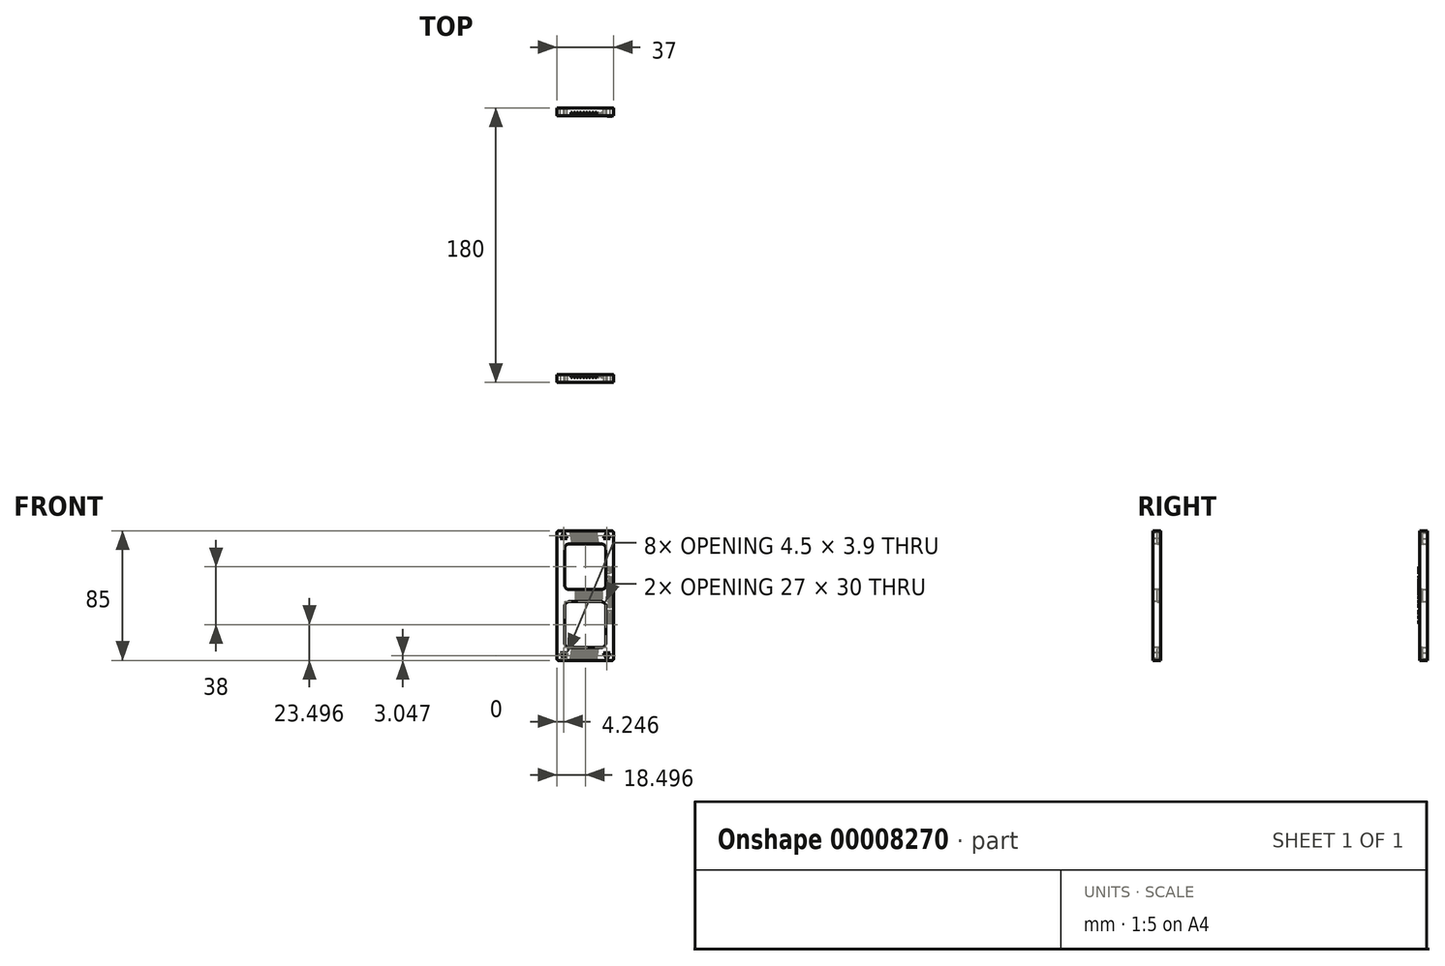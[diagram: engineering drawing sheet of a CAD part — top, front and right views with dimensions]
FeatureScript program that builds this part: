
annotation { "Feature Type Name" : "Feature", "Feature Type Description" : "" }
export const myFeature = defineFeature(function(context is Context, id is Id, definition is map)
    precondition{}
    {
        {
            var Q0;
            Q0=qCreatedBy(makeId("Front.planeOp"),FACE);
            var sketch = newSketch(context, id + "F0", { "sketchPlane" : qUnion([Q0])});
            skLineSegment(sketch, "E0.bottom", {"start": v(-64.24, 55.65) * mm, "end": v(-29.24, 55.65) * mm});
            skLineSegment(sketch, "E0.top", {"start": v(-64.24, -29.35) * mm, "end": v(-29.24, -29.35) * mm});
            skLineSegment(sketch, "E0.left", {"start": v(-65.24, 54.65) * mm, "end": v(-65.24, -28.35) * mm});
            skLineSegment(sketch, "E0.right", {"start": v(-28.24, 54.65) * mm, "end": v(-28.24, -28.35) * mm});
            skLineSegment(sketch, "E1.bottom", {"start": v(-57.24, 47.15) * mm, "end": v(-36.24, 47.15) * mm});
            skLineSegment(sketch, "E1.top", {"start": v(-57.24, 17.15) * mm, "end": v(-36.24, 17.15) * mm});
            skLineSegment(sketch, "E1.left", {"start": v(-60.24, 44.15) * mm, "end": v(-60.24, 20.15) * mm});
            skLineSegment(sketch, "E1.right", {"start": v(-33.24, 44.15) * mm, "end": v(-33.24, 20.15) * mm});
            skPoint(sketch, "E2", {"position": v(-65.24, 13.15) * mm});
            skPoint(sketch, "E3", {"position": v(-28.24, 13.15) * mm});
            skLineSegment(sketch, "E4", {"start": v(-65.24, 13.15) * mm, "end": v(-28.24, 13.15) * mm, "construction": true});
            skPoint(sketch, "E5", {"position": v(-46.74, 13.15) * mm});
            skPoint(sketch, "E6", {"position": v(-46.74, 17.15) * mm});
            skPoint(sketch, "E7", {"position": v(-46.74, 47.15) * mm});
            skLineSegment(sketch, "E8", {"start": v(-46.74, -29.35) * mm, "end": v(-46.74, 55.65) * mm, "construction": true});
            skLineSegment(sketch, "E9.MirrorCS", {"start": v(-57.24, 9.15) * mm, "end": v(-36.24, 9.15) * mm});
            skLineSegment(sketch, "E10.MirrorCS", {"start": v(-33.24, -17.85) * mm, "end": v(-33.24, 6.15) * mm});
            skLineSegment(sketch, "E11.MirrorCS", {"start": v(-57.24, -20.85) * mm, "end": v(-36.24, -20.85) * mm});
            skLineSegment(sketch, "E12.MirrorCS", {"start": v(-60.24, -17.85) * mm, "end": v(-60.24, 6.15) * mm});
            skLineSegment(sketch, "E13", {"start": v(-61, 54.54) * mm, "end": v(-63.24, 50.65) * mm});
            skLineSegment(sketch, "E14", {"start": v(-63.24, 50.65) * mm, "end": v(-58.74, 50.65) * mm});
            skLineSegment(sketch, "E15", {"start": v(-58.74, 50.65) * mm, "end": v(-61, 54.54) * mm});
            skLineSegment(sketch, "E16.MirrorCS", {"start": v(-32.5, 54.54) * mm, "end": v(-30.24, 50.65) * mm});
            skLineSegment(sketch, "E17.MirrorCS", {"start": v(-34.74, 50.65) * mm, "end": v(-32.5, 54.54) * mm});
            skLineSegment(sketch, "E18.MirrorCS", {"start": v(-30.24, 50.65) * mm, "end": v(-34.74, 50.65) * mm});
            skLineSegment(sketch, "E19.MirrorCS", {"start": v(-32.5, -28.25) * mm, "end": v(-30.24, -24.35) * mm});
            skLineSegment(sketch, "E20.MirrorCS", {"start": v(-34.74, -24.35) * mm, "end": v(-32.5, -28.25) * mm});
            skLineSegment(sketch, "E21.MirrorCS", {"start": v(-30.24, -24.35) * mm, "end": v(-34.74, -24.35) * mm});
            skLineSegment(sketch, "E22.MirrorCS", {"start": v(-58.74, -24.35) * mm, "end": v(-61, -28.25) * mm});
            skLineSegment(sketch, "E23.MirrorCS", {"start": v(-61, -28.25) * mm, "end": v(-63.24, -24.35) * mm});
            skLineSegment(sketch, "E24.MirrorCS", {"start": v(-63.24, -24.35) * mm, "end": v(-58.74, -24.35) * mm});
            skPoint(sketch, "E25.visualSharp", {"position": v(-60.24, 47.15) * mm});
            skArc(sketch, "E25.filletArc", {"start": v(-57.24, 47.15) * mm, "mid": v(-59.37, 46.27) * mm, "end": v(-60.24, 44.15) * mm});
            skPoint(sketch, "E26.visualSharp", {"position": v(-33.24, 47.15) * mm});
            skArc(sketch, "E26.filletArc", {"start": v(-33.24, 44.15) * mm, "mid": v(-34.12, 46.27) * mm, "end": v(-36.24, 47.15) * mm});
            skPoint(sketch, "E27.visualSharp", {"position": v(-33.24, 17.15) * mm});
            skArc(sketch, "E27.filletArc", {"start": v(-36.24, 17.15) * mm, "mid": v(-34.12, 18.02) * mm, "end": v(-33.24, 20.15) * mm});
            skPoint(sketch, "E28.visualSharp", {"position": v(-60.24, 17.15) * mm});
            skArc(sketch, "E28.filletArc", {"start": v(-60.24, 20.15) * mm, "mid": v(-59.37, 18.02) * mm, "end": v(-57.24, 17.15) * mm});
            skPoint(sketch, "E29.visualSharp", {"position": v(-33.24, 9.15) * mm});
            skArc(sketch, "E29.filletArc", {"start": v(-33.24, 6.15) * mm, "mid": v(-34.12, 8.27) * mm, "end": v(-36.24, 9.15) * mm});
            skPoint(sketch, "E30.visualSharp", {"position": v(-33.24, -20.85) * mm});
            skArc(sketch, "E30.filletArc", {"start": v(-36.24, -20.85) * mm, "mid": v(-34.12, -19.98) * mm, "end": v(-33.24, -17.85) * mm});
            skPoint(sketch, "E31.visualSharp", {"position": v(-60.24, -20.85) * mm});
            skArc(sketch, "E31.filletArc", {"start": v(-60.24, -17.85) * mm, "mid": v(-59.37, -19.98) * mm, "end": v(-57.24, -20.85) * mm});
            skPoint(sketch, "E32.visualSharp", {"position": v(-60.24, 9.15) * mm});
            skArc(sketch, "E32.filletArc", {"start": v(-57.24, 9.15) * mm, "mid": v(-59.37, 8.27) * mm, "end": v(-60.24, 6.15) * mm});
            skPoint(sketch, "E33.visualSharp", {"position": v(-28.24, 55.65) * mm});
            skArc(sketch, "E33.filletArc", {"start": v(-28.24, 54.65) * mm, "mid": v(-28.54, 55.35) * mm, "end": v(-29.24, 55.65) * mm});
            skPoint(sketch, "E34.visualSharp", {"position": v(-28.24, -29.35) * mm});
            skArc(sketch, "E34.filletArc", {"start": v(-29.24, -29.35) * mm, "mid": v(-28.54, -29.06) * mm, "end": v(-28.24, -28.35) * mm});
            skPoint(sketch, "E35.visualSharp", {"position": v(-65.24, -29.35) * mm});
            skArc(sketch, "E35.filletArc", {"start": v(-65.24, -28.35) * mm, "mid": v(-64.95, -29.06) * mm, "end": v(-64.24, -29.35) * mm});
            skPoint(sketch, "E36.visualSharp", {"position": v(-65.24, 55.65) * mm});
            skArc(sketch, "E36.filletArc", {"start": v(-64.24, 55.65) * mm, "mid": v(-64.95, 55.35) * mm, "end": v(-65.24, 54.65) * mm});
            skSolve(sketch);
        }
        {
            var Q0;
            Q0 = qSketchRegion(id + "F0", true);
            extrude(context, id + "F1", {"entities" : qUnion([Q0]), "depth" : 5 * mm});
        }
        {
            var Q0;
            Q0=makeQuery(id+"F1.opExtrude","CAP_FACE",FACE,{"disambiguationData":[OSD([sQuery(id+"F0.wireOp",EDGE,"E0.bottom"),sQuery(id+"F0.wireOp",EDGE,"E0.top"),sQuery(id+"F0.wireOp",EDGE,"E0.left"),sQuery(id+"F0.wireOp",EDGE,"E0.right")])],"isStart":false});
            var sketch = newSketch(context, id + "F2", { "sketchPlane" : qUnion([Q0])});
            skArc(sketch, "E37", {"start": v(-56.24, -29.35) * mm, "mid": v(-52.51, 13.15) * mm, "end": v(-56.24, 55.65) * mm});
            skLineSegment(sketch, "E38", {"start": v(-56.24, 55.65) * mm, "end": v(-56.24, -29.35) * mm, "construction": true});
            skPoint(sketch, "E39", {"position": v(-56.24, 13.15) * mm});
            skLineSegment(sketch, "E40", {"start": v(-56.24, 13.15) * mm, "end": v(-296.24, 13.15) * mm, "construction": true});
            skArc(sketch, "E41.1.0.0", {"start": v(-55.34, -29.35) * mm, "mid": v(-51.61, 13.15) * mm, "end": v(-55.34, 55.65) * mm});
            skLineSegment(sketch, "E41.direction1", {"start": v(-296.24, 13.15) * mm, "end": v(-295.34, 13.15) * mm, "construction": true});
            skLineSegment(sketch, "E42", {"start": v(-56.24, 55.65) * mm, "end": v(-55.34, 55.65) * mm});
            skLineSegment(sketch, "E43", {"start": v(-56.24, -29.35) * mm, "end": v(-55.34, -29.35) * mm});
            skArc(sketch, "E44.1.0.0", {"start": v(-54.24, -29.35) * mm, "mid": v(-50.51, 13.15) * mm, "end": v(-54.24, 55.65) * mm});
            skArc(sketch, "E44.1.0.1", {"start": v(-53.34, -29.35) * mm, "mid": v(-49.61, 13.15) * mm, "end": v(-53.34, 55.65) * mm});
            skLineSegment(sketch, "E44.1.0.2", {"start": v(-54.24, 55.65) * mm, "end": v(-53.34, 55.65) * mm});
            skLineSegment(sketch, "E44.1.0.3", {"start": v(-54.24, -29.35) * mm, "end": v(-53.34, -29.35) * mm});
            skArc(sketch, "E44.2.0.0", {"start": v(-52.24, -29.35) * mm, "mid": v(-48.51, 13.15) * mm, "end": v(-52.24, 55.65) * mm});
            skArc(sketch, "E44.2.0.1", {"start": v(-51.34, -29.35) * mm, "mid": v(-47.61, 13.15) * mm, "end": v(-51.34, 55.65) * mm});
            skLineSegment(sketch, "E44.2.0.2", {"start": v(-52.24, 55.65) * mm, "end": v(-51.34, 55.65) * mm});
            skLineSegment(sketch, "E44.2.0.3", {"start": v(-52.24, -29.35) * mm, "end": v(-51.34, -29.35) * mm});
            skArc(sketch, "E44.3.0.0", {"start": v(-50.24, -29.35) * mm, "mid": v(-46.51, 13.15) * mm, "end": v(-50.24, 55.65) * mm});
            skArc(sketch, "E44.3.0.1", {"start": v(-49.34, -29.35) * mm, "mid": v(-45.61, 13.15) * mm, "end": v(-49.34, 55.65) * mm});
            skLineSegment(sketch, "E44.3.0.2", {"start": v(-50.24, 55.65) * mm, "end": v(-49.34, 55.65) * mm});
            skLineSegment(sketch, "E44.3.0.3", {"start": v(-50.24, -29.35) * mm, "end": v(-49.34, -29.35) * mm});
            skArc(sketch, "E44.4.0.0", {"start": v(-48.24, -29.35) * mm, "mid": v(-44.51, 13.15) * mm, "end": v(-48.24, 55.65) * mm});
            skArc(sketch, "E44.4.0.1", {"start": v(-47.34, -29.35) * mm, "mid": v(-43.61, 13.15) * mm, "end": v(-47.34, 55.65) * mm});
            skLineSegment(sketch, "E44.4.0.2", {"start": v(-48.24, 55.65) * mm, "end": v(-47.34, 55.65) * mm});
            skLineSegment(sketch, "E44.4.0.3", {"start": v(-48.24, -29.35) * mm, "end": v(-47.34, -29.35) * mm});
            skArc(sketch, "E44.5.0.0", {"start": v(-46.24, -29.35) * mm, "mid": v(-42.51, 13.15) * mm, "end": v(-46.24, 55.65) * mm});
            skArc(sketch, "E44.5.0.1", {"start": v(-45.34, -29.35) * mm, "mid": v(-41.61, 13.15) * mm, "end": v(-45.34, 55.65) * mm});
            skLineSegment(sketch, "E44.5.0.2", {"start": v(-46.24, 55.65) * mm, "end": v(-45.34, 55.65) * mm});
            skLineSegment(sketch, "E44.5.0.3", {"start": v(-46.24, -29.35) * mm, "end": v(-45.34, -29.35) * mm});
            skArc(sketch, "E44.6.0.0", {"start": v(-44.24, -29.35) * mm, "mid": v(-40.51, 13.15) * mm, "end": v(-44.24, 55.65) * mm});
            skArc(sketch, "E44.6.0.1", {"start": v(-43.34, -29.35) * mm, "mid": v(-39.61, 13.15) * mm, "end": v(-43.34, 55.65) * mm});
            skLineSegment(sketch, "E44.6.0.2", {"start": v(-44.24, 55.65) * mm, "end": v(-43.34, 55.65) * mm});
            skLineSegment(sketch, "E44.6.0.3", {"start": v(-44.24, -29.35) * mm, "end": v(-43.34, -29.35) * mm});
            skArc(sketch, "E44.7.0.0", {"start": v(-42.24, -29.35) * mm, "mid": v(-38.51, 13.15) * mm, "end": v(-42.24, 55.65) * mm});
            skArc(sketch, "E44.7.0.1", {"start": v(-41.34, -29.35) * mm, "mid": v(-37.61, 13.15) * mm, "end": v(-41.34, 55.65) * mm});
            skLineSegment(sketch, "E44.7.0.2", {"start": v(-42.24, 55.65) * mm, "end": v(-41.34, 55.65) * mm});
            skLineSegment(sketch, "E44.7.0.3", {"start": v(-42.24, -29.35) * mm, "end": v(-41.34, -29.35) * mm});
            skLineSegment(sketch, "E44.direction1", {"start": v(-296.24, 13.15) * mm, "end": v(-294.24, 13.15) * mm, "construction": true});
            skArc(sketch, "E45.0.8.0", {"start": v(-40.24, -29.35) * mm, "mid": v(-36.51, 13.15) * mm, "end": v(-40.24, 55.65) * mm});
            skArc(sketch, "E45.4.8.0", {"start": v(-39.34, -29.35) * mm, "mid": v(-35.61, 13.15) * mm, "end": v(-39.34, 55.65) * mm});
            skLineSegment(sketch, "E45.8.8.0", {"start": v(-40.24, 55.65) * mm, "end": v(-39.34, 55.65) * mm});
            skLineSegment(sketch, "E45.11.8.0", {"start": v(-40.24, -29.35) * mm, "end": v(-39.34, -29.35) * mm});
            skSolve(sketch);
        }
        {
            var Q0;
            Q0 = qSketchRegion(id + "F2", true);
            extrude(context, id + "F3", {"entities" : qUnion([Q0]), "operationType" : NewBodyOperationType.REMOVE, "oppositeDirection" : true, "depth" : 2 * mm});
        }
        {
            var Q0;
            {var subQ1=sQuery(id+"F0.wireOp",EDGE,"E0.top");var subQ2=sQuery(id+"F2.wireOp",EDGE,"E37");Q0=makeQuery(id+"F3.boolean.opBoolean","COPY",EDGE,{"disambiguationData":[TD([makeQuery(id+"F1.opExtrude","SWEPT_FACE",FACE,{"disambiguationData":[OSD([subQ1])]})])],"derivedFrom":makeQuery(id+"F3.opExtrude","CAP_EDGE",EDGE,{"disambiguationData":[OSD([subQ2])],"isStart":true})});}
            var Q1;
            {var subQ1=sQuery(id+"F0.wireOp",EDGE,"E0.top");var subQ2=sQuery(id+"F2.wireOp",EDGE,"E41.1.0.0");Q1=makeQuery(id+"F3.boolean.opBoolean","COPY",EDGE,{"disambiguationData":[TD([makeQuery(id+"F1.opExtrude","SWEPT_FACE",FACE,{"disambiguationData":[OSD([subQ1])]})])],"derivedFrom":makeQuery(id+"F3.opExtrude","CAP_EDGE",EDGE,{"disambiguationData":[OSD([subQ2])],"isStart":true})});}
            var Q2;
            {var subQ1=sQuery(id+"F0.wireOp",EDGE,"E0.top");var subQ2=sQuery(id+"F2.wireOp",EDGE,"E44.1.0.0");Q2=makeQuery(id+"F3.boolean.opBoolean","COPY",EDGE,{"disambiguationData":[TD([makeQuery(id+"F1.opExtrude","SWEPT_FACE",FACE,{"disambiguationData":[OSD([subQ1])]})])],"derivedFrom":makeQuery(id+"F3.opExtrude","CAP_EDGE",EDGE,{"disambiguationData":[OSD([subQ2])],"isStart":true})});}
            var Q3;
            {var subQ1=sQuery(id+"F0.wireOp",EDGE,"E0.top");var subQ2=sQuery(id+"F2.wireOp",EDGE,"E44.1.0.1");Q3=makeQuery(id+"F3.boolean.opBoolean","COPY",EDGE,{"disambiguationData":[TD([makeQuery(id+"F1.opExtrude","SWEPT_FACE",FACE,{"disambiguationData":[OSD([subQ1])]})])],"derivedFrom":makeQuery(id+"F3.opExtrude","CAP_EDGE",EDGE,{"disambiguationData":[OSD([subQ2])],"isStart":true})});}
            var Q4;
            {var subQ1=sQuery(id+"F0.wireOp",EDGE,"E0.top");var subQ2=sQuery(id+"F2.wireOp",EDGE,"E44.2.0.0");Q4=makeQuery(id+"F3.boolean.opBoolean","COPY",EDGE,{"disambiguationData":[TD([makeQuery(id+"F1.opExtrude","SWEPT_FACE",FACE,{"disambiguationData":[OSD([subQ1])]})])],"derivedFrom":makeQuery(id+"F3.opExtrude","CAP_EDGE",EDGE,{"disambiguationData":[OSD([subQ2])],"isStart":true})});}
            var Q5;
            {var subQ1=sQuery(id+"F0.wireOp",EDGE,"E0.top");var subQ2=sQuery(id+"F2.wireOp",EDGE,"E44.2.0.1");Q5=makeQuery(id+"F3.boolean.opBoolean","COPY",EDGE,{"disambiguationData":[TD([makeQuery(id+"F1.opExtrude","SWEPT_FACE",FACE,{"disambiguationData":[OSD([subQ1])]})])],"derivedFrom":makeQuery(id+"F3.opExtrude","CAP_EDGE",EDGE,{"disambiguationData":[OSD([subQ2])],"isStart":true})});}
            var Q6;
            {var subQ1=sQuery(id+"F0.wireOp",EDGE,"E0.top");var subQ2=sQuery(id+"F2.wireOp",EDGE,"E44.3.0.0");Q6=makeQuery(id+"F3.boolean.opBoolean","COPY",EDGE,{"disambiguationData":[TD([makeQuery(id+"F1.opExtrude","SWEPT_FACE",FACE,{"disambiguationData":[OSD([subQ1])]})])],"derivedFrom":makeQuery(id+"F3.opExtrude","CAP_EDGE",EDGE,{"disambiguationData":[OSD([subQ2])],"isStart":true})});}
            var Q7;
            {var subQ1=sQuery(id+"F0.wireOp",EDGE,"E0.top");var subQ2=sQuery(id+"F2.wireOp",EDGE,"E44.3.0.1");Q7=makeQuery(id+"F3.boolean.opBoolean","COPY",EDGE,{"disambiguationData":[TD([makeQuery(id+"F1.opExtrude","SWEPT_FACE",FACE,{"disambiguationData":[OSD([subQ1])]})])],"derivedFrom":makeQuery(id+"F3.opExtrude","CAP_EDGE",EDGE,{"disambiguationData":[OSD([subQ2])],"isStart":true})});}
            var Q8;
            {var subQ1=sQuery(id+"F0.wireOp",EDGE,"E0.top");var subQ2=sQuery(id+"F2.wireOp",EDGE,"E44.4.0.0");Q8=makeQuery(id+"F3.boolean.opBoolean","COPY",EDGE,{"disambiguationData":[TD([makeQuery(id+"F1.opExtrude","SWEPT_FACE",FACE,{"disambiguationData":[OSD([subQ1])]})])],"derivedFrom":makeQuery(id+"F3.opExtrude","CAP_EDGE",EDGE,{"disambiguationData":[OSD([subQ2])],"isStart":true})});}
            var Q9;
            {var subQ1=sQuery(id+"F0.wireOp",EDGE,"E0.top");var subQ2=sQuery(id+"F2.wireOp",EDGE,"E44.4.0.1");Q9=makeQuery(id+"F3.boolean.opBoolean","COPY",EDGE,{"disambiguationData":[TD([makeQuery(id+"F1.opExtrude","SWEPT_FACE",FACE,{"disambiguationData":[OSD([subQ1])]})])],"derivedFrom":makeQuery(id+"F3.opExtrude","CAP_EDGE",EDGE,{"disambiguationData":[OSD([subQ2])],"isStart":true})});}
            var Q10;
            {var subQ1=sQuery(id+"F0.wireOp",EDGE,"E0.top");var subQ2=sQuery(id+"F2.wireOp",EDGE,"E44.5.0.0");Q10=makeQuery(id+"F3.boolean.opBoolean","COPY",EDGE,{"disambiguationData":[TD([makeQuery(id+"F1.opExtrude","SWEPT_FACE",FACE,{"disambiguationData":[OSD([subQ1])]})])],"derivedFrom":makeQuery(id+"F3.opExtrude","CAP_EDGE",EDGE,{"disambiguationData":[OSD([subQ2])],"isStart":true})});}
            var Q11;
            {var subQ1=sQuery(id+"F0.wireOp",EDGE,"E0.top");var subQ2=sQuery(id+"F2.wireOp",EDGE,"E44.5.0.1");Q11=makeQuery(id+"F3.boolean.opBoolean","COPY",EDGE,{"disambiguationData":[TD([makeQuery(id+"F1.opExtrude","SWEPT_FACE",FACE,{"disambiguationData":[OSD([subQ1])]})])],"derivedFrom":makeQuery(id+"F3.opExtrude","CAP_EDGE",EDGE,{"disambiguationData":[OSD([subQ2])],"isStart":true})});}
            var Q12;
            {var subQ1=sQuery(id+"F0.wireOp",EDGE,"E0.top");var subQ2=sQuery(id+"F2.wireOp",EDGE,"E44.6.0.0");Q12=makeQuery(id+"F3.boolean.opBoolean","COPY",EDGE,{"disambiguationData":[TD([makeQuery(id+"F1.opExtrude","SWEPT_FACE",FACE,{"disambiguationData":[OSD([subQ1])]})])],"derivedFrom":makeQuery(id+"F3.opExtrude","CAP_EDGE",EDGE,{"disambiguationData":[OSD([subQ2])],"isStart":true})});}
            var Q13;
            {var subQ1=sQuery(id+"F0.wireOp",EDGE,"E0.top");var subQ2=sQuery(id+"F2.wireOp",EDGE,"E44.6.0.1");Q13=makeQuery(id+"F3.boolean.opBoolean","COPY",EDGE,{"disambiguationData":[TD([makeQuery(id+"F1.opExtrude","SWEPT_FACE",FACE,{"disambiguationData":[OSD([subQ1])]})])],"derivedFrom":makeQuery(id+"F3.opExtrude","CAP_EDGE",EDGE,{"disambiguationData":[OSD([subQ2])],"isStart":true})});}
            var Q14;
            {var subQ1=sQuery(id+"F0.wireOp",EDGE,"E0.top");var subQ2=sQuery(id+"F2.wireOp",EDGE,"E44.7.0.0");Q14=makeQuery(id+"F3.boolean.opBoolean","COPY",EDGE,{"disambiguationData":[TD([makeQuery(id+"F1.opExtrude","SWEPT_FACE",FACE,{"disambiguationData":[OSD([subQ1])]})])],"derivedFrom":makeQuery(id+"F3.opExtrude","CAP_EDGE",EDGE,{"disambiguationData":[OSD([subQ2])],"isStart":true})});}
            var Q15;
            {var subQ1=sQuery(id+"F0.wireOp",EDGE,"E0.top");var subQ2=sQuery(id+"F2.wireOp",EDGE,"E44.7.0.1");Q15=makeQuery(id+"F3.boolean.opBoolean","COPY",EDGE,{"disambiguationData":[TD([makeQuery(id+"F1.opExtrude","SWEPT_FACE",FACE,{"disambiguationData":[OSD([subQ1])]})])],"derivedFrom":makeQuery(id+"F3.opExtrude","CAP_EDGE",EDGE,{"disambiguationData":[OSD([subQ2])],"isStart":true})});}
            var Q16;
            {var subQ1=sQuery(id+"F0.wireOp",EDGE,"E0.top");var subQ2=sQuery(id+"F2.wireOp",EDGE,"E45.0.8.0");Q16=makeQuery(id+"F3.boolean.opBoolean","COPY",EDGE,{"disambiguationData":[TD([makeQuery(id+"F1.opExtrude","SWEPT_FACE",FACE,{"disambiguationData":[OSD([subQ1])]})])],"derivedFrom":makeQuery(id+"F3.opExtrude","CAP_EDGE",EDGE,{"disambiguationData":[OSD([subQ2])],"isStart":true})});}
            var Q17;
            {var subQ1=sQuery(id+"F0.wireOp",EDGE,"E1.top");var subQ2=sQuery(id+"F2.wireOp",EDGE,"E41.1.0.0");Q17=makeQuery(id+"F3.boolean.opBoolean","COPY",EDGE,{"disambiguationData":[TD([makeQuery(id+"F1.opExtrude","SWEPT_FACE",FACE,{"disambiguationData":[OSD([subQ1])]})])],"derivedFrom":makeQuery(id+"F3.opExtrude","CAP_EDGE",EDGE,{"disambiguationData":[OSD([subQ2])],"isStart":true})});}
            var Q18;
            {var subQ1=sQuery(id+"F0.wireOp",EDGE,"E1.top");var subQ2=sQuery(id+"F2.wireOp",EDGE,"E44.1.0.0");Q18=makeQuery(id+"F3.boolean.opBoolean","COPY",EDGE,{"disambiguationData":[TD([makeQuery(id+"F1.opExtrude","SWEPT_FACE",FACE,{"disambiguationData":[OSD([subQ1])]})])],"derivedFrom":makeQuery(id+"F3.opExtrude","CAP_EDGE",EDGE,{"disambiguationData":[OSD([subQ2])],"isStart":true})});}
            var Q19;
            {var subQ1=sQuery(id+"F0.wireOp",EDGE,"E1.top");var subQ2=sQuery(id+"F2.wireOp",EDGE,"E44.1.0.1");Q19=makeQuery(id+"F3.boolean.opBoolean","COPY",EDGE,{"disambiguationData":[TD([makeQuery(id+"F1.opExtrude","SWEPT_FACE",FACE,{"disambiguationData":[OSD([subQ1])]})])],"derivedFrom":makeQuery(id+"F3.opExtrude","CAP_EDGE",EDGE,{"disambiguationData":[OSD([subQ2])],"isStart":true})});}
            var Q20;
            {var subQ1=sQuery(id+"F0.wireOp",EDGE,"E1.top");var subQ2=sQuery(id+"F2.wireOp",EDGE,"E44.2.0.0");Q20=makeQuery(id+"F3.boolean.opBoolean","COPY",EDGE,{"disambiguationData":[TD([makeQuery(id+"F1.opExtrude","SWEPT_FACE",FACE,{"disambiguationData":[OSD([subQ1])]})])],"derivedFrom":makeQuery(id+"F3.opExtrude","CAP_EDGE",EDGE,{"disambiguationData":[OSD([subQ2])],"isStart":true})});}
            var Q21;
            {var subQ1=sQuery(id+"F0.wireOp",EDGE,"E1.top");var subQ2=sQuery(id+"F2.wireOp",EDGE,"E44.2.0.1");Q21=makeQuery(id+"F3.boolean.opBoolean","COPY",EDGE,{"disambiguationData":[TD([makeQuery(id+"F1.opExtrude","SWEPT_FACE",FACE,{"disambiguationData":[OSD([subQ1])]})])],"derivedFrom":makeQuery(id+"F3.opExtrude","CAP_EDGE",EDGE,{"disambiguationData":[OSD([subQ2])],"isStart":true})});}
            var Q22;
            {var subQ1=sQuery(id+"F0.wireOp",EDGE,"E1.top");var subQ2=sQuery(id+"F2.wireOp",EDGE,"E44.3.0.0");Q22=makeQuery(id+"F3.boolean.opBoolean","COPY",EDGE,{"disambiguationData":[TD([makeQuery(id+"F1.opExtrude","SWEPT_FACE",FACE,{"disambiguationData":[OSD([subQ1])]})])],"derivedFrom":makeQuery(id+"F3.opExtrude","CAP_EDGE",EDGE,{"disambiguationData":[OSD([subQ2])],"isStart":true})});}
            var Q23;
            {var subQ1=sQuery(id+"F0.wireOp",EDGE,"E1.top");var subQ2=sQuery(id+"F2.wireOp",EDGE,"E44.3.0.1");Q23=makeQuery(id+"F3.boolean.opBoolean","COPY",EDGE,{"disambiguationData":[TD([makeQuery(id+"F1.opExtrude","SWEPT_FACE",FACE,{"disambiguationData":[OSD([subQ1])]})])],"derivedFrom":makeQuery(id+"F3.opExtrude","CAP_EDGE",EDGE,{"disambiguationData":[OSD([subQ2])],"isStart":true})});}
            var Q24;
            {var subQ1=sQuery(id+"F0.wireOp",EDGE,"E1.top");var subQ2=sQuery(id+"F2.wireOp",EDGE,"E44.4.0.0");Q24=makeQuery(id+"F3.boolean.opBoolean","COPY",EDGE,{"disambiguationData":[TD([makeQuery(id+"F1.opExtrude","SWEPT_FACE",FACE,{"disambiguationData":[OSD([subQ1])]})])],"derivedFrom":makeQuery(id+"F3.opExtrude","CAP_EDGE",EDGE,{"disambiguationData":[OSD([subQ2])],"isStart":true})});}
            var Q25;
            {var subQ1=sQuery(id+"F0.wireOp",EDGE,"E1.top");var subQ2=sQuery(id+"F2.wireOp",EDGE,"E44.4.0.1");Q25=makeQuery(id+"F3.boolean.opBoolean","COPY",EDGE,{"disambiguationData":[TD([makeQuery(id+"F1.opExtrude","SWEPT_FACE",FACE,{"disambiguationData":[OSD([subQ1])]})])],"derivedFrom":makeQuery(id+"F3.opExtrude","CAP_EDGE",EDGE,{"disambiguationData":[OSD([subQ2])],"isStart":true})});}
            var Q26;
            {var subQ1=sQuery(id+"F0.wireOp",EDGE,"E1.top");var subQ2=sQuery(id+"F2.wireOp",EDGE,"E44.5.0.0");Q26=makeQuery(id+"F3.boolean.opBoolean","COPY",EDGE,{"disambiguationData":[TD([makeQuery(id+"F1.opExtrude","SWEPT_FACE",FACE,{"disambiguationData":[OSD([subQ1])]})])],"derivedFrom":makeQuery(id+"F3.opExtrude","CAP_EDGE",EDGE,{"disambiguationData":[OSD([subQ2])],"isStart":true})});}
            var Q27;
            {var subQ1=sQuery(id+"F0.wireOp",EDGE,"E1.top");var subQ2=sQuery(id+"F2.wireOp",EDGE,"E44.5.0.1");Q27=makeQuery(id+"F3.boolean.opBoolean","COPY",EDGE,{"disambiguationData":[TD([makeQuery(id+"F1.opExtrude","SWEPT_FACE",FACE,{"disambiguationData":[OSD([subQ1])]})])],"derivedFrom":makeQuery(id+"F3.opExtrude","CAP_EDGE",EDGE,{"disambiguationData":[OSD([subQ2])],"isStart":true})});}
            var Q28;
            {var subQ1=sQuery(id+"F0.wireOp",EDGE,"E1.top");var subQ2=sQuery(id+"F2.wireOp",EDGE,"E44.6.0.0");Q28=makeQuery(id+"F3.boolean.opBoolean","COPY",EDGE,{"disambiguationData":[TD([makeQuery(id+"F1.opExtrude","SWEPT_FACE",FACE,{"disambiguationData":[OSD([subQ1])]})])],"derivedFrom":makeQuery(id+"F3.opExtrude","CAP_EDGE",EDGE,{"disambiguationData":[OSD([subQ2])],"isStart":true})});}
            var Q29;
            {var subQ1=sQuery(id+"F0.wireOp",EDGE,"E1.top");var subQ2=sQuery(id+"F2.wireOp",EDGE,"E44.6.0.1");Q29=makeQuery(id+"F3.boolean.opBoolean","COPY",EDGE,{"disambiguationData":[TD([makeQuery(id+"F1.opExtrude","SWEPT_FACE",FACE,{"disambiguationData":[OSD([subQ1])]})])],"derivedFrom":makeQuery(id+"F3.opExtrude","CAP_EDGE",EDGE,{"disambiguationData":[OSD([subQ2])],"isStart":true})});}
            var Q30;
            {var subQ1=sQuery(id+"F0.wireOp",EDGE,"E1.top");var subQ2=sQuery(id+"F2.wireOp",EDGE,"E44.7.0.0");Q30=makeQuery(id+"F3.boolean.opBoolean","COPY",EDGE,{"disambiguationData":[TD([makeQuery(id+"F1.opExtrude","SWEPT_FACE",FACE,{"disambiguationData":[OSD([subQ1])]})])],"derivedFrom":makeQuery(id+"F3.opExtrude","CAP_EDGE",EDGE,{"disambiguationData":[OSD([subQ2])],"isStart":true})});}
            var Q31;
            {var subQ1=sQuery(id+"F0.wireOp",EDGE,"E1.top");var subQ2=sQuery(id+"F2.wireOp",EDGE,"E44.7.0.1");Q31=makeQuery(id+"F3.boolean.opBoolean","COPY",EDGE,{"disambiguationData":[TD([makeQuery(id+"F1.opExtrude","SWEPT_FACE",FACE,{"disambiguationData":[OSD([subQ1])]})])],"derivedFrom":makeQuery(id+"F3.opExtrude","CAP_EDGE",EDGE,{"disambiguationData":[OSD([subQ2])],"isStart":true})});}
            var Q32;
            {var subQ1=sQuery(id+"F0.wireOp",EDGE,"E1.top");var subQ2=sQuery(id+"F2.wireOp",EDGE,"E45.0.8.0");Q32=makeQuery(id+"F3.boolean.opBoolean","COPY",EDGE,{"disambiguationData":[TD([makeQuery(id+"F1.opExtrude","SWEPT_FACE",FACE,{"disambiguationData":[OSD([subQ1])]})])],"derivedFrom":makeQuery(id+"F3.opExtrude","CAP_EDGE",EDGE,{"disambiguationData":[OSD([subQ2])],"isStart":true})});}
            var Q33;
            {var subQ0=sQuery(id+"F0.wireOp",EDGE,"E0.bottom");var subQ1=sQuery(id+"F2.wireOp",EDGE,"E37");Q33=makeQuery(id+"F3.boolean.opBoolean","COPY",EDGE,{"disambiguationData":[TD([makeQuery(id+"F1.opExtrude","SWEPT_FACE",FACE,{"disambiguationData":[OSD([subQ0])]})])],"derivedFrom":makeQuery(id+"F3.opExtrude","CAP_EDGE",EDGE,{"disambiguationData":[OSD([subQ1])],"isStart":true})});}
            var Q34;
            {var subQ1=sQuery(id+"F0.wireOp",EDGE,"E1.top");var subQ2=sQuery(id+"F2.wireOp",EDGE,"E37");Q34=makeQuery(id+"F3.boolean.opBoolean","COPY",EDGE,{"disambiguationData":[TD([makeQuery(id+"F1.opExtrude","SWEPT_FACE",FACE,{"disambiguationData":[OSD([subQ1])]})])],"derivedFrom":makeQuery(id+"F3.opExtrude","CAP_EDGE",EDGE,{"disambiguationData":[OSD([subQ2])],"isStart":true})});}
            var Q35;
            {var subQ1=sQuery(id+"F0.wireOp",EDGE,"E27.filletArc");var subQ2=sQuery(id+"F2.wireOp",EDGE,"E45.4.8.0");Q35=makeQuery(id+"F3.boolean.opBoolean","COPY",EDGE,{"disambiguationData":[TD([makeQuery(id+"F1.opExtrude","SWEPT_FACE",FACE,{"disambiguationData":[OSD([subQ1])]})])],"derivedFrom":makeQuery(id+"F3.opExtrude","CAP_EDGE",EDGE,{"disambiguationData":[OSD([subQ2])],"isStart":true})});}
            var Q36;
            {var subQ1=sQuery(id+"F0.wireOp",EDGE,"E0.top");var subQ2=sQuery(id+"F2.wireOp",EDGE,"E45.4.8.0");Q36=makeQuery(id+"F3.boolean.opBoolean","COPY",EDGE,{"disambiguationData":[TD([makeQuery(id+"F1.opExtrude","SWEPT_FACE",FACE,{"disambiguationData":[OSD([subQ1])]})])],"derivedFrom":makeQuery(id+"F3.opExtrude","CAP_EDGE",EDGE,{"disambiguationData":[OSD([subQ2])],"isStart":true})});}
            var Q37;
            Q37=makeQuery(id+"F3.boolean.opBoolean","INTERSECT",EDGE,{"derivedFrom":[makeQuery(id+"F1.opExtrude","SWEPT_FACE",FACE,{"disambiguationData":[OSD([sQuery(id+"F0.wireOp",EDGE,"E1.bottom")])]}),makeQuery(id+"F3.opExtrude","SWEPT_FACE",FACE,{"disambiguationData":[OSD([sQuery(id+"F2.wireOp",EDGE,"E37")])]})]});
            var Q38;
            {var subQ0=sQuery(id+"F0.wireOp",EDGE,"E0.bottom");var subQ2=sQuery(id+"F2.wireOp",EDGE,"E44.1.0.0");Q38=makeQuery(id+"F3.boolean.opBoolean","COPY",EDGE,{"disambiguationData":[TD([makeQuery(id+"F1.opExtrude","SWEPT_FACE",FACE,{"disambiguationData":[OSD([subQ0])]})])],"derivedFrom":makeQuery(id+"F3.opExtrude","CAP_EDGE",EDGE,{"disambiguationData":[OSD([subQ2])],"isStart":true})});}
            var Q39;
            {var subQ0=sQuery(id+"F0.wireOp",EDGE,"E0.bottom");var subQ1=sQuery(id+"F2.wireOp",EDGE,"E44.1.0.1");Q39=makeQuery(id+"F3.boolean.opBoolean","COPY",EDGE,{"disambiguationData":[TD([makeQuery(id+"F1.opExtrude","SWEPT_FACE",FACE,{"disambiguationData":[OSD([subQ0])]})])],"derivedFrom":makeQuery(id+"F3.opExtrude","CAP_EDGE",EDGE,{"disambiguationData":[OSD([subQ1])],"isStart":true})});}
            var Q40;
            {var subQ0=sQuery(id+"F0.wireOp",EDGE,"E0.bottom");var subQ2=sQuery(id+"F2.wireOp",EDGE,"E44.2.0.1");Q40=makeQuery(id+"F3.boolean.opBoolean","COPY",EDGE,{"disambiguationData":[TD([makeQuery(id+"F1.opExtrude","SWEPT_FACE",FACE,{"disambiguationData":[OSD([subQ0])]})])],"derivedFrom":makeQuery(id+"F3.opExtrude","CAP_EDGE",EDGE,{"disambiguationData":[OSD([subQ2])],"isStart":true})});}
            var Q41;
            {var subQ0=sQuery(id+"F0.wireOp",EDGE,"E0.bottom");var subQ1=sQuery(id+"F2.wireOp",EDGE,"E44.3.0.0");Q41=makeQuery(id+"F3.boolean.opBoolean","COPY",EDGE,{"disambiguationData":[TD([makeQuery(id+"F1.opExtrude","SWEPT_FACE",FACE,{"disambiguationData":[OSD([subQ0])]})])],"derivedFrom":makeQuery(id+"F3.opExtrude","CAP_EDGE",EDGE,{"disambiguationData":[OSD([subQ1])],"isStart":true})});}
            var Q42;
            {var subQ0=sQuery(id+"F0.wireOp",EDGE,"E0.bottom");var subQ1=sQuery(id+"F2.wireOp",EDGE,"E44.4.0.0");Q42=makeQuery(id+"F3.boolean.opBoolean","COPY",EDGE,{"disambiguationData":[TD([makeQuery(id+"F1.opExtrude","SWEPT_FACE",FACE,{"disambiguationData":[OSD([subQ0])]})])],"derivedFrom":makeQuery(id+"F3.opExtrude","CAP_EDGE",EDGE,{"disambiguationData":[OSD([subQ1])],"isStart":true})});}
            var Q43;
            {var subQ0=sQuery(id+"F0.wireOp",EDGE,"E0.bottom");var subQ2=sQuery(id+"F2.wireOp",EDGE,"E44.4.0.1");Q43=makeQuery(id+"F3.boolean.opBoolean","COPY",EDGE,{"disambiguationData":[TD([makeQuery(id+"F1.opExtrude","SWEPT_FACE",FACE,{"disambiguationData":[OSD([subQ0])]})])],"derivedFrom":makeQuery(id+"F3.opExtrude","CAP_EDGE",EDGE,{"disambiguationData":[OSD([subQ2])],"isStart":true})});}
            var Q44;
            {var subQ0=sQuery(id+"F0.wireOp",EDGE,"E0.bottom");var subQ2=sQuery(id+"F2.wireOp",EDGE,"E44.5.0.0");Q44=makeQuery(id+"F3.boolean.opBoolean","COPY",EDGE,{"disambiguationData":[TD([makeQuery(id+"F1.opExtrude","SWEPT_FACE",FACE,{"disambiguationData":[OSD([subQ0])]})])],"derivedFrom":makeQuery(id+"F3.opExtrude","CAP_EDGE",EDGE,{"disambiguationData":[OSD([subQ2])],"isStart":true})});}
            var Q45;
            {var subQ0=sQuery(id+"F0.wireOp",EDGE,"E0.bottom");var subQ2=sQuery(id+"F2.wireOp",EDGE,"E44.5.0.1");Q45=makeQuery(id+"F3.boolean.opBoolean","COPY",EDGE,{"disambiguationData":[TD([makeQuery(id+"F1.opExtrude","SWEPT_FACE",FACE,{"disambiguationData":[OSD([subQ0])]})])],"derivedFrom":makeQuery(id+"F3.opExtrude","CAP_EDGE",EDGE,{"disambiguationData":[OSD([subQ2])],"isStart":true})});}
            var Q46;
            {var subQ0=sQuery(id+"F0.wireOp",EDGE,"E0.bottom");var subQ2=sQuery(id+"F2.wireOp",EDGE,"E44.6.0.0");Q46=makeQuery(id+"F3.boolean.opBoolean","COPY",EDGE,{"disambiguationData":[TD([makeQuery(id+"F1.opExtrude","SWEPT_FACE",FACE,{"disambiguationData":[OSD([subQ0])]})])],"derivedFrom":makeQuery(id+"F3.opExtrude","CAP_EDGE",EDGE,{"disambiguationData":[OSD([subQ2])],"isStart":true})});}
            var Q47;
            {var subQ0=sQuery(id+"F0.wireOp",EDGE,"E0.bottom");var subQ2=sQuery(id+"F2.wireOp",EDGE,"E44.6.0.1");Q47=makeQuery(id+"F3.boolean.opBoolean","COPY",EDGE,{"disambiguationData":[TD([makeQuery(id+"F1.opExtrude","SWEPT_FACE",FACE,{"disambiguationData":[OSD([subQ0])]})])],"derivedFrom":makeQuery(id+"F3.opExtrude","CAP_EDGE",EDGE,{"disambiguationData":[OSD([subQ2])],"isStart":true})});}
            var Q48;
            {var subQ0=sQuery(id+"F0.wireOp",EDGE,"E0.bottom");var subQ2=sQuery(id+"F2.wireOp",EDGE,"E44.7.0.0");Q48=makeQuery(id+"F3.boolean.opBoolean","COPY",EDGE,{"disambiguationData":[TD([makeQuery(id+"F1.opExtrude","SWEPT_FACE",FACE,{"disambiguationData":[OSD([subQ0])]})])],"derivedFrom":makeQuery(id+"F3.opExtrude","CAP_EDGE",EDGE,{"disambiguationData":[OSD([subQ2])],"isStart":true})});}
            var Q49;
            {var subQ0=sQuery(id+"F0.wireOp",EDGE,"E0.bottom");var subQ2=sQuery(id+"F2.wireOp",EDGE,"E44.7.0.1");Q49=makeQuery(id+"F3.boolean.opBoolean","COPY",EDGE,{"disambiguationData":[TD([makeQuery(id+"F1.opExtrude","SWEPT_FACE",FACE,{"disambiguationData":[OSD([subQ0])]})])],"derivedFrom":makeQuery(id+"F3.opExtrude","CAP_EDGE",EDGE,{"disambiguationData":[OSD([subQ2])],"isStart":true})});}
            var Q50;
            {var subQ0=sQuery(id+"F0.wireOp",EDGE,"E0.bottom");var subQ2=sQuery(id+"F2.wireOp",EDGE,"E45.0.8.0");Q50=makeQuery(id+"F3.boolean.opBoolean","COPY",EDGE,{"disambiguationData":[TD([makeQuery(id+"F1.opExtrude","SWEPT_FACE",FACE,{"disambiguationData":[OSD([subQ0])]})])],"derivedFrom":makeQuery(id+"F3.opExtrude","CAP_EDGE",EDGE,{"disambiguationData":[OSD([subQ2])],"isStart":true})});}
            var Q51;
            {var subQ0=sQuery(id+"F0.wireOp",EDGE,"E0.bottom");var subQ2=sQuery(id+"F2.wireOp",EDGE,"E45.4.8.0");Q51=makeQuery(id+"F3.boolean.opBoolean","COPY",EDGE,{"disambiguationData":[TD([makeQuery(id+"F1.opExtrude","SWEPT_FACE",FACE,{"disambiguationData":[OSD([subQ0])]})])],"derivedFrom":makeQuery(id+"F3.opExtrude","CAP_EDGE",EDGE,{"disambiguationData":[OSD([subQ2])],"isStart":true})});}
            var Q52;
            {var subQ0=sQuery(id+"F0.wireOp",EDGE,"E0.bottom");var subQ1=sQuery(id+"F2.wireOp",EDGE,"E44.4.0.0");Q52=makeQuery(id+"F3.boolean.opBoolean","COPY",EDGE,{"disambiguationData":[TD([makeQuery(id+"F1.opExtrude","SWEPT_FACE",FACE,{"disambiguationData":[OSD([subQ0])]})])],"derivedFrom":makeQuery(id+"F3.opExtrude","CAP_EDGE",EDGE,{"disambiguationData":[OSD([subQ1])],"isStart":true})});}
            var Q53;
            {var subQ0=sQuery(id+"F0.wireOp",EDGE,"E0.bottom");var subQ1=sQuery(id+"F2.wireOp",EDGE,"E41.1.0.0");Q53=makeQuery(id+"F3.boolean.opBoolean","COPY",EDGE,{"disambiguationData":[TD([makeQuery(id+"F1.opExtrude","SWEPT_FACE",FACE,{"disambiguationData":[OSD([subQ0])]})])],"derivedFrom":makeQuery(id+"F3.opExtrude","CAP_EDGE",EDGE,{"disambiguationData":[OSD([subQ1])],"isStart":true})});}
            var Q54;
            {var subQ0=sQuery(id+"F0.wireOp",EDGE,"E0.bottom");var subQ2=sQuery(id+"F2.wireOp",EDGE,"E44.3.0.1");Q54=makeQuery(id+"F3.boolean.opBoolean","COPY",EDGE,{"disambiguationData":[TD([makeQuery(id+"F1.opExtrude","SWEPT_FACE",FACE,{"disambiguationData":[OSD([subQ0])]})])],"derivedFrom":makeQuery(id+"F3.opExtrude","CAP_EDGE",EDGE,{"disambiguationData":[OSD([subQ2])],"isStart":true})});}
            chamfer(context, id + "F4", {"entities" : qUnion([Q0, Q1, Q2, Q3, Q4, Q5, Q6, Q7, Q8, Q9, Q10, Q11, Q12, Q13, Q14, Q15, Q16, Q17, Q18, Q19, Q20, Q21, Q22, Q23, Q24, Q25, Q26, Q27, Q28, Q29, Q30, Q31, Q32, Q33, Q34, Q35, Q36, Q37, Q38, Q39, Q40, Q41, Q42, Q43, Q44, Q45, Q46, Q47, Q48, Q49, Q50, Q51, Q52, Q53, Q54]), "width" : 0.4 * mm, "tangentPropagation" : true});
        }
        {
            var Q0;
            {var subQ0=sQuery(id+"F0.wireOp",EDGE,"E0.bottom");var subQ1=sQuery(id+"F0.wireOp",EDGE,"E0.top");var subQ2=sQuery(id+"F0.wireOp",EDGE,"E0.right");var subQ3=sQuery(id+"F0.wireOp",EDGE,"E1.bottom");var subQ4=sQuery(id+"F0.wireOp",EDGE,"E1.right");var subQ5=sQuery(id+"F0.wireOp",EDGE,"E10.MirrorCS");var subQ6=sQuery(id+"F0.wireOp",EDGE,"E11.MirrorCS");var subQ7=sQuery(id+"F0.wireOp",EDGE,"E16.MirrorCS");var subQ8=sQuery(id+"F0.wireOp",EDGE,"E17.MirrorCS");var subQ9=sQuery(id+"F0.wireOp",EDGE,"E18.MirrorCS");var subQ10=sQuery(id+"F0.wireOp",EDGE,"E19.MirrorCS");var subQ11=sQuery(id+"F0.wireOp",EDGE,"E20.MirrorCS");var subQ12=sQuery(id+"F0.wireOp",EDGE,"E21.MirrorCS");var subQ13=sQuery(id+"F0.wireOp",EDGE,"E26.filletArc");var subQ14=sQuery(id+"F0.wireOp",EDGE,"E27.filletArc");var subQ15=sQuery(id+"F0.wireOp",EDGE,"E29.filletArc");var subQ16=sQuery(id+"F0.wireOp",EDGE,"E30.filletArc");var subQ17=sQuery(id+"F0.wireOp",EDGE,"E33.filletArc");var subQ18=sQuery(id+"F0.wireOp",EDGE,"E34.filletArc");Q0=makeQuery(id+"F3.boolean.opBoolean","SPLIT",FACE,{"disambiguationData":[TD([makeQuery(id+"F1.opExtrude","SWEPT_FACE",FACE,{"disambiguationData":[OSD([subQ0])]}),makeQuery(id+"F1.opExtrude","SWEPT_FACE",FACE,{"disambiguationData":[OSD([subQ1])]}),makeQuery(id+"F1.opExtrude","SWEPT_FACE",FACE,{"disambiguationData":[OSD([subQ2])]}),makeQuery(id+"F1.opExtrude","SWEPT_FACE",FACE,{"disambiguationData":[OSD([subQ3])]}),makeQuery(id+"F1.opExtrude","SWEPT_FACE",FACE,{"disambiguationData":[OSD([subQ4])]}),makeQuery(id+"F1.opExtrude","SWEPT_FACE",FACE,{"disambiguationData":[OSD([subQ5])]}),makeQuery(id+"F1.opExtrude","SWEPT_FACE",FACE,{"disambiguationData":[OSD([subQ6])]}),makeQuery(id+"F1.opExtrude","SWEPT_FACE",FACE,{"disambiguationData":[OSD([subQ7])]}),makeQuery(id+"F1.opExtrude","SWEPT_FACE",FACE,{"disambiguationData":[OSD([subQ8])]}),makeQuery(id+"F1.opExtrude","SWEPT_FACE",FACE,{"disambiguationData":[OSD([subQ9])]}),makeQuery(id+"F1.opExtrude","SWEPT_FACE",FACE,{"disambiguationData":[OSD([subQ10])]}),makeQuery(id+"F1.opExtrude","SWEPT_FACE",FACE,{"disambiguationData":[OSD([subQ11])]}),makeQuery(id+"F1.opExtrude","SWEPT_FACE",FACE,{"disambiguationData":[OSD([subQ12])]}),makeQuery(id+"F1.opExtrude","SWEPT_FACE",FACE,{"disambiguationData":[OSD([subQ13])]}),makeQuery(id+"F1.opExtrude","SWEPT_FACE",FACE,{"disambiguationData":[OSD([subQ14])]}),makeQuery(id+"F1.opExtrude","SWEPT_FACE",FACE,{"disambiguationData":[OSD([subQ15])]}),makeQuery(id+"F1.opExtrude","SWEPT_FACE",FACE,{"disambiguationData":[OSD([subQ16])]}),makeQuery(id+"F1.opExtrude","SWEPT_FACE",FACE,{"disambiguationData":[OSD([subQ17])]}),makeQuery(id+"F1.opExtrude","SWEPT_FACE",FACE,{"disambiguationData":[OSD([subQ18])]}),makeQuery(id+"F3.opExtrude","SWEPT_FACE",FACE,{"disambiguationData":[OSD([sQuery(id+"F2.wireOp",EDGE,"E45.4.8.0")])]})])],"derivedFrom":makeQuery(id+"F1.opExtrude","CAP_FACE",FACE,{"disambiguationData":[OSD([subQ0,subQ1,sQuery(id+"F0.wireOp",EDGE,"E0.left"),subQ2,subQ3,sQuery(id+"F0.wireOp",EDGE,"E1.top"),sQuery(id+"F0.wireOp",EDGE,"E1.left"),subQ4,sQuery(id+"F0.wireOp",EDGE,"E9.MirrorCS"),subQ5,subQ6,sQuery(id+"F0.wireOp",EDGE,"E12.MirrorCS"),sQuery(id+"F0.wireOp",EDGE,"E13"),sQuery(id+"F0.wireOp",EDGE,"E14"),sQuery(id+"F0.wireOp",EDGE,"E15"),subQ7,subQ8,subQ9,subQ10,subQ11,subQ12,sQuery(id+"F0.wireOp",EDGE,"E22.MirrorCS"),sQuery(id+"F0.wireOp",EDGE,"E23.MirrorCS"),sQuery(id+"F0.wireOp",EDGE,"E24.MirrorCS"),sQuery(id+"F0.wireOp",EDGE,"E25.filletArc"),subQ13,subQ14,sQuery(id+"F0.wireOp",EDGE,"E28.filletArc"),subQ15,subQ16,sQuery(id+"F0.wireOp",EDGE,"E31.filletArc"),sQuery(id+"F0.wireOp",EDGE,"E32.filletArc"),subQ17,subQ18,sQuery(id+"F0.wireOp",EDGE,"E35.filletArc"),sQuery(id+"F0.wireOp",EDGE,"E36.filletArc")])],"isStart":false})});}
            var sketch = newSketch(context, id + "F5", { "sketchPlane" : qUnion([Q0])});
            skText(sketch, "E46", { "text": "HHO Generator v2", "fontName": "OpenSans-Bold.ttf"});
            skPoint(sketch, "E47", {"position": v(-30.74, 32.07) * mm});
            skPoint(sketch, "E48", {"position": v(-30.74, 13.15) * mm});
            skLineSegment(sketch, "E49", {"start": v(-30.74, -29.35) * mm, "end": v(-30.74, 55.65) * mm, "construction": true});
            skLineSegment(sketch, "E50", {"start": v(-33.24, 5.18) * mm, "end": v(-33.24, 21.57) * mm, "construction": true});
            skLineSegment(sketch, "E51", {"start": v(-28.24, 13.15) * mm, "end": v(-33.24, 13.15) * mm, "construction": true});
            skPoint(sketch, "E52", {"position": v(-32.24, 13.15) * mm});
            const initialGuessF5  = {"E46": [-0.02924, -0.00578, 0, 1, 0.003]};
            skSetInitialGuess(sketch, initialGuessF5);
            skSolve(sketch);
        }
        {
            var Q0;
            Q0=qCreatedBy(makeId("Front.planeOp"),FACE);
            cPlane(context, id + "F6", {"entities" : qUnion([Q0]), "cplaneType" : CPlaneType.OFFSET, "offset" : 90 * mm, "width" : 150 * mm, "height" : 150 * mm});
        }
        {
            var Q0;
            Q0=makeQuery(id+"F1.opExtrude","SWEPT_BODY",BODY,{"disambiguationData":[OSD([sQuery(id+"F0.wireOp",EDGE,"E0.bottom"),sQuery(id+"F0.wireOp",EDGE,"E0.top"),sQuery(id+"F0.wireOp",EDGE,"E0.left"),sQuery(id+"F0.wireOp",EDGE,"E0.right"),sQuery(id+"F0.wireOp",EDGE,"E1.bottom"),sQuery(id+"F0.wireOp",EDGE,"E1.top"),sQuery(id+"F0.wireOp",EDGE,"E1.left"),sQuery(id+"F0.wireOp",EDGE,"E1.right"),sQuery(id+"F0.wireOp",EDGE,"E9.MirrorCS"),sQuery(id+"F0.wireOp",EDGE,"E10.MirrorCS"),sQuery(id+"F0.wireOp",EDGE,"E11.MirrorCS"),sQuery(id+"F0.wireOp",EDGE,"E12.MirrorCS")])]});
            var Q1;
            Q1=qCreatedBy(id+"F6.planeOp",FACE);
            mirror(context, id + "F7", {"entities" : qUnion([Q0]), "mirrorPlane" : qUnion([Q1])});
        }
        {
            var Q0;
            Q0 = qSketchRegion(id + "F5", true);
            extrude(context, id + "F8", {"entities" : qUnion([Q0]), "operationType" : NewBodyOperationType.ADD, "depth" : 0.5 * mm});
        }
    });
